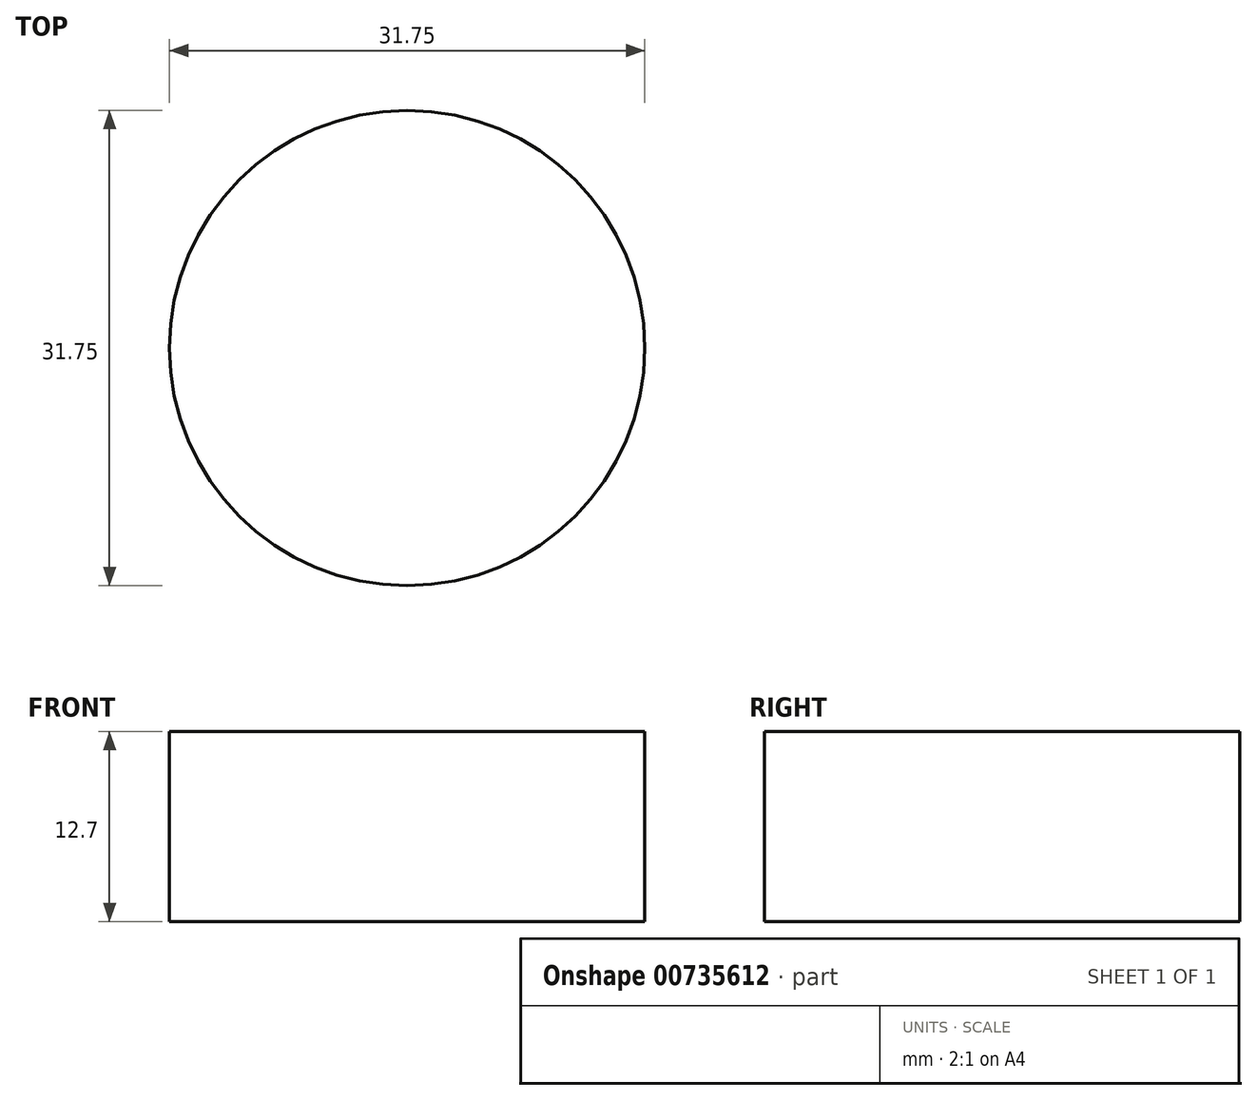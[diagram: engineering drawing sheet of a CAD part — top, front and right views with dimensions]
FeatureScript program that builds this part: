
annotation { "Feature Type Name" : "Feature", "Feature Type Description" : "" }
export const myFeature = defineFeature(function(context is Context, id is Id, definition is map)
    precondition{}
    {
        {
            var Q0;
            Q0=qCreatedBy(makeId("Top.planeOp"),FACE);
            var sketch = newSketch(context, id + "F0", { "sketchPlane" : qUnion([Q0])});
            skLineSegment(sketch, "E0.bottom", {"start": v(63.5, -63.5) * mm, "end": v(-63.5, -63.5) * mm});
            skLineSegment(sketch, "E0.left", {"start": v(63.5, -63.5) * mm, "end": v(63.5, 63.5) * mm});
            skLineSegment(sketch, "E0.right", {"start": v(-63.5, -63.5) * mm, "end": v(-63.5, 63.5) * mm});
            skPoint(sketch, "E0.middle", {"position": v(0, 0) * mm});
            skLineSegment(sketch, "E1", {"start": v(-63.5, 88.9) * mm, "end": v(63.5, 88.9) * mm});
            skLineSegment(sketch, "E2", {"start": v(-63.5, 63.5) * mm, "end": v(-63.5, 88.9) * mm});
            skLineSegment(sketch, "E3", {"start": v(63.5, 63.5) * mm, "end": v(63.5, 88.9) * mm});
            skSolve(sketch);
        }
        {
            var Q0;
            Q0 = qSketchRegion(id + "F0", true);
            extrude(context, id + "F1", {"entities" : qUnion([Q0]), "oppositeDirection" : true, "depth" : 12.7 * mm, "offsetDistance" : 25.4 * mm});
        }
        {
            var Q0;
            Q0=makeQuery(id+"F1.opExtrude","CAP_FACE",FACE,{"disambiguationData":[OSD([sQuery(id+"F0.wireOp",EDGE,"E0.bottom"),sQuery(id+"F0.wireOp",EDGE,"E0.top"),sQuery(id+"F0.wireOp",EDGE,"E0.left"),sQuery(id+"F0.wireOp",EDGE,"E0.right")])],"isStart":true});
            var sketch = newSketch(context, id + "F2", { "sketchPlane" : qUnion([Q0])});
            skCircle(sketch, "E4", {"center": v(-33.34, 30.16) * mm, "radius": 15.88 * mm});
            skCircle(sketch, "E5.MirrorC", {"center": v(33.34, 30.16) * mm, "radius": 15.88 * mm});
            skSolve(sketch);
        }
        {
            var Q0;
            Q0=makeQuery(id+"F2.imprint","IMPRINT",FACE,{"disambiguationData":[TD([[makeQuery(id+"F2.imprint","IMPRINT",EDGE,{"derivedFrom":sQuery(id+"F2.wireOp",EDGE,"E4")}),1.0]])]});
            var Q1;
            Q1=makeQuery(id+"F2.imprint","IMPRINT",FACE,{"disambiguationData":[TD([[makeQuery(id+"F2.imprint","IMPRINT",EDGE,{"derivedFrom":sQuery(id+"F2.wireOp",EDGE,"E5.MirrorC")}),-1.0]])]});
            var Q2;
            Q2=sQuery(id+"F2.wireOp",EDGE,"E4");
            var Q3;
            Q3=sQuery(id+"F2.wireOp",EDGE,"E5.MirrorC");
            extrude(context, id + "F3", {"entities" : qUnion([Q0, Q1]), "operationType" : NewBodyOperationType.REMOVE, "surfaceEntities" : qUnion([Q2, Q3]), "oppositeDirection" : true, "depth" : 25.4 * mm, "offsetDistance" : 25.4 * mm});
        }
    });
